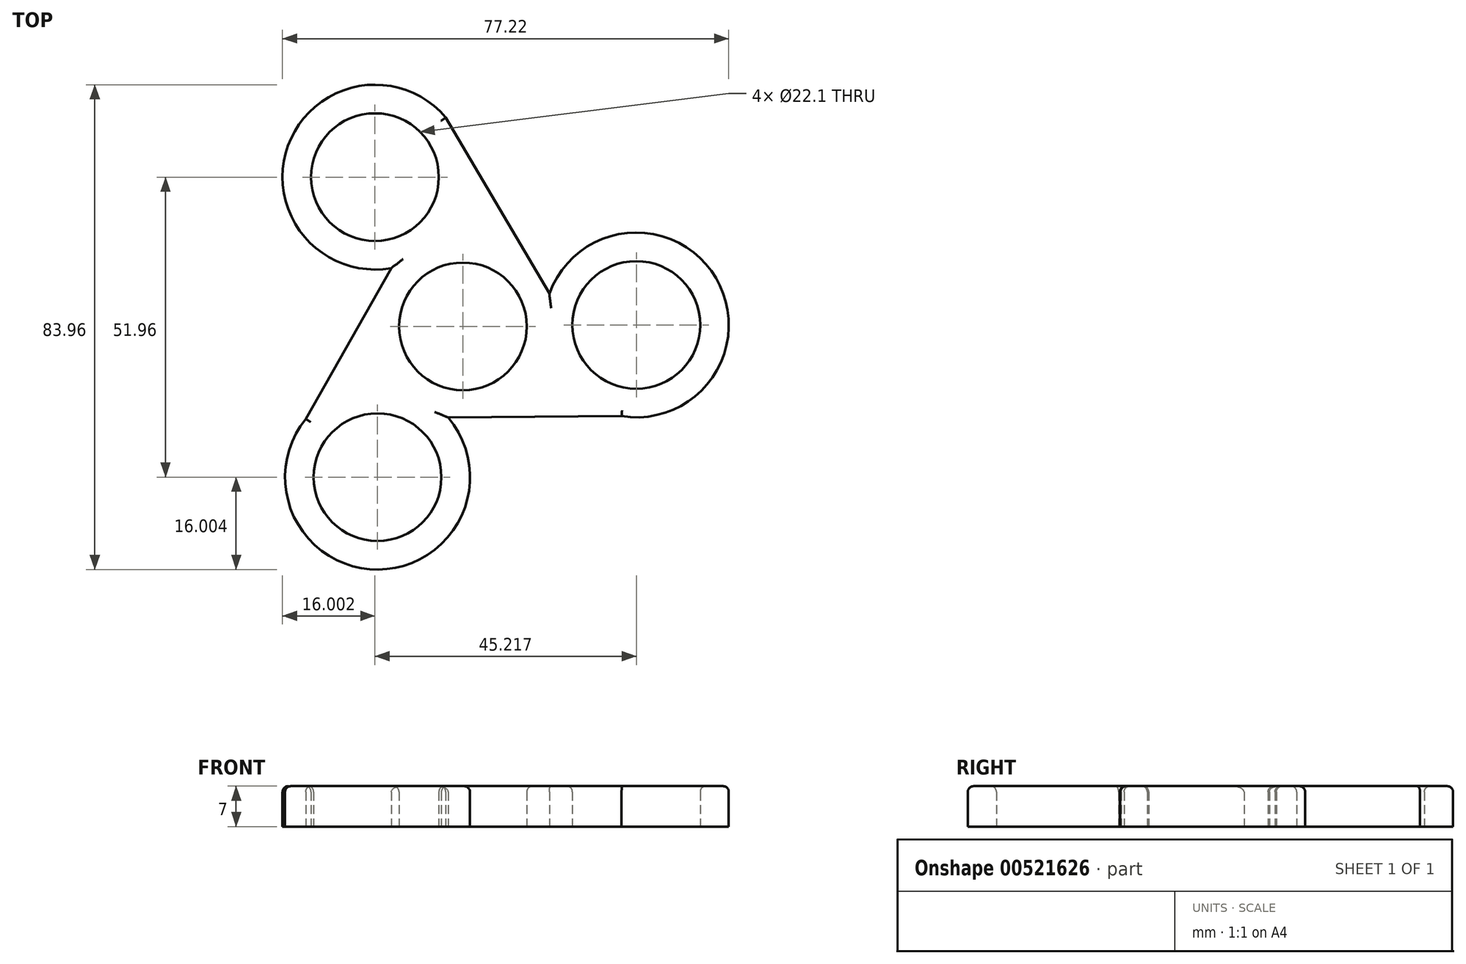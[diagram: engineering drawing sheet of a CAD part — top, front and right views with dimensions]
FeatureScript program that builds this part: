
annotation { "Feature Type Name" : "Feature", "Feature Type Description" : "" }
export const myFeature = defineFeature(function(context is Context, id is Id, definition is map)
    precondition{}
    {
        {
            var Q0;
            Q0=qCreatedBy(makeId("Top.planeOp"),FACE);
            var sketch = newSketch(context, id + "F0", { "sketchPlane" : qUnion([Q0])});
            skCircle(sketch, "E0", {"center": v(0, 0) * mm, "radius": 11.05 * mm});
            skCircle(sketch, "E1", {"center": v(0, 0) * mm, "radius": 16 * mm});
            skLineSegment(sketch, "E2", {"start": v(0, 0) * mm, "end": v(-14.78, -26.1) * mm});
            skLineSegment(sketch, "E3", {"start": v(0, 0) * mm, "end": v(30, 0.25) * mm});
            skLineSegment(sketch, "E4", {"start": v(0, 0) * mm, "end": v(-15.22, 25.85) * mm});
            skCircle(sketch, "E5", {"center": v(-15.22, 25.85) * mm, "radius": 11.05 * mm});
            skCircle(sketch, "E6", {"center": v(-14.78, -26.1) * mm, "radius": 11.05 * mm});
            skCircle(sketch, "E7", {"center": v(30, 0.25) * mm, "radius": 11.05 * mm});
            skCircle(sketch, "E8", {"center": v(-14.78, -26.1) * mm, "radius": 16 * mm});
            skCircle(sketch, "E9", {"center": v(-15.22, 25.85) * mm, "radius": 16 * mm});
            skCircle(sketch, "E10", {"center": v(30, 0.25) * mm, "radius": 16 * mm});
            skLineSegment(sketch, "E11", {"start": v(14.95, 5.7) * mm, "end": v(-2.98, 36.16) * mm});
            skLineSegment(sketch, "E12", {"start": v(-12.4, 10.1) * mm, "end": v(-27.19, -16) * mm});
            skLineSegment(sketch, "E13", {"start": v(-2.55, -15.8) * mm, "end": v(27.45, -15.54) * mm});
            skSolve(sketch);
        }
        {
            var Q0;
            {var subQ0=sQuery(id+"F0.wireOp",EDGE,"E4");var subQ1=sQuery(id+"F0.wireOp",EDGE,"E0");var subQ2=makeQuery(id+"F0.imprint","INTERSECT",VERTEX,{"derivedFrom":[subQ1,subQ0]});Q0=makeQuery(id+"F0.imprint","IMPRINT",FACE,{"disambiguationData":[TD([[makeQuery(id+"F0.imprint","IMPRINT",EDGE,{"disambiguationData":[TD([[subQ2,-1.0]])],"derivedFrom":subQ1}),-1.0]])]});}
            var Q1;
            Q1=makeQuery(id+"F0.imprint","IMPRINT",FACE,{"disambiguationData":[TD([[makeQuery(id+"F0.imprint","IMPRINT",EDGE,{"derivedFrom":sQuery(id+"F0.wireOp",EDGE,"E6")}),-1.0]])]});
            var Q2;
            {var subQ0=sQuery(id+"F0.wireOp",EDGE,"E12");var subQ1=sQuery(id+"F0.wireOp",EDGE,"E1");var subQ2=makeQuery(id+"F0.imprint","INTERSECT",VERTEX,{"derivedFrom":[subQ1,subQ0]});Q2=makeQuery(id+"F0.imprint","IMPRINT",FACE,{"disambiguationData":[TD([[makeQuery(id+"F0.imprint","IMPRINT",EDGE,{"disambiguationData":[TD([[subQ2,-1.0]])],"derivedFrom":subQ1}),-1.0]])]});}
            var Q3;
            {var subQ0=sQuery(id+"F0.wireOp",EDGE,"E3");var subQ1=sQuery(id+"F0.wireOp",EDGE,"E0");var subQ2=makeQuery(id+"F0.imprint","INTERSECT",VERTEX,{"derivedFrom":[subQ1,subQ0]});Q3=makeQuery(id+"F0.imprint","IMPRINT",FACE,{"disambiguationData":[TD([[makeQuery(id+"F0.imprint","IMPRINT",EDGE,{"disambiguationData":[TD([[subQ2,1.0]])],"derivedFrom":subQ1}),-1.0]])]});}
            var Q4;
            {var subQ1=sQuery(id+"F0.wireOp",EDGE,"E1");var subQ3=sQuery(id+"F0.wireOp",EDGE,"E2");var subQ4=makeQuery(id+"F0.imprint","INTERSECT",VERTEX,{"derivedFrom":[subQ1,subQ3]});Q4=makeQuery(id+"F0.imprint","IMPRINT",FACE,{"disambiguationData":[TD([[makeQuery(id+"F0.imprint","IMPRINT",EDGE,{"disambiguationData":[TD([[subQ4,1.0]])],"derivedFrom":subQ3}),1.0]])]});}
            var Q5;
            {var subQ0=sQuery(id+"F0.wireOp",EDGE,"E4");var subQ1=sQuery(id+"F0.wireOp",EDGE,"E0");var subQ2=makeQuery(id+"F0.imprint","INTERSECT",VERTEX,{"derivedFrom":[subQ1,subQ0]});Q5=makeQuery(id+"F0.imprint","IMPRINT",FACE,{"disambiguationData":[TD([[makeQuery(id+"F0.imprint","IMPRINT",EDGE,{"disambiguationData":[TD([[subQ2,1.0]])],"derivedFrom":subQ1}),-1.0]])]});}
            var Q6;
            {var subQ1=sQuery(id+"F0.wireOp",EDGE,"E1");var subQ3=sQuery(id+"F0.wireOp",EDGE,"E3");var subQ4=makeQuery(id+"F0.imprint","INTERSECT",VERTEX,{"derivedFrom":[subQ1,subQ3]});Q6=makeQuery(id+"F0.imprint","IMPRINT",FACE,{"disambiguationData":[TD([[makeQuery(id+"F0.imprint","IMPRINT",EDGE,{"disambiguationData":[TD([[subQ4,1.0]])],"derivedFrom":subQ3}),1.0]])]});}
            var Q7;
            Q7=makeQuery(id+"F0.imprint","IMPRINT",FACE,{"disambiguationData":[TD([[makeQuery(id+"F0.imprint","IMPRINT",EDGE,{"derivedFrom":sQuery(id+"F0.wireOp",EDGE,"E7")}),-1.0]])]});
            var Q8;
            Q8=makeQuery(id+"F0.imprint","IMPRINT",FACE,{"disambiguationData":[TD([[makeQuery(id+"F0.imprint","IMPRINT",EDGE,{"derivedFrom":sQuery(id+"F0.wireOp",EDGE,"E5")}),-1.0]])]});
            var Q9;
            {var subQ0=sQuery(id+"F0.wireOp",EDGE,"E11");var subQ1=sQuery(id+"F0.wireOp",EDGE,"E1");var subQ2=makeQuery(id+"F0.imprint","INTERSECT",VERTEX,{"derivedFrom":[subQ1,subQ0]});Q9=makeQuery(id+"F0.imprint","IMPRINT",FACE,{"disambiguationData":[TD([[makeQuery(id+"F0.imprint","IMPRINT",EDGE,{"disambiguationData":[TD([[subQ2,-1.0]])],"derivedFrom":subQ1}),-1.0]])]});}
            var Q10;
            {var subQ0=sQuery(id+"F0.wireOp",EDGE,"E13");var subQ1=sQuery(id+"F0.wireOp",EDGE,"E1");var subQ2=makeQuery(id+"F0.imprint","INTERSECT",VERTEX,{"derivedFrom":[subQ1,subQ0]});Q10=makeQuery(id+"F0.imprint","IMPRINT",FACE,{"disambiguationData":[TD([[makeQuery(id+"F0.imprint","IMPRINT",EDGE,{"disambiguationData":[TD([[subQ2,-1.0]])],"derivedFrom":subQ1}),-1.0]])]});}
            var Q11;
            {var subQ0=sQuery(id+"F0.wireOp",EDGE,"E3");var subQ1=sQuery(id+"F0.wireOp",EDGE,"E1");var subQ2=makeQuery(id+"F0.imprint","INTERSECT",VERTEX,{"derivedFrom":[subQ1,subQ0]});Q11=makeQuery(id+"F0.imprint","IMPRINT",FACE,{"disambiguationData":[TD([[makeQuery(id+"F0.imprint","IMPRINT",EDGE,{"disambiguationData":[TD([[subQ2,1.0]])],"derivedFrom":subQ1}),1.0]])]});}
            var Q12;
            {var subQ0=sQuery(id+"F0.wireOp",EDGE,"E2");var subQ1=sQuery(id+"F0.wireOp",EDGE,"E1");var subQ2=makeQuery(id+"F0.imprint","INTERSECT",VERTEX,{"derivedFrom":[subQ1,subQ0]});Q12=makeQuery(id+"F0.imprint","IMPRINT",FACE,{"disambiguationData":[TD([[makeQuery(id+"F0.imprint","IMPRINT",EDGE,{"disambiguationData":[TD([[subQ2,1.0]])],"derivedFrom":subQ1}),1.0]])]});}
            var Q13;
            {var subQ1=sQuery(id+"F0.wireOp",EDGE,"E1");var subQ3=sQuery(id+"F0.wireOp",EDGE,"E4");var subQ4=makeQuery(id+"F0.imprint","INTERSECT",VERTEX,{"derivedFrom":[subQ1,subQ3]});Q13=makeQuery(id+"F0.imprint","IMPRINT",FACE,{"disambiguationData":[TD([[makeQuery(id+"F0.imprint","IMPRINT",EDGE,{"disambiguationData":[TD([[subQ4,1.0]])],"derivedFrom":subQ3}),1.0]])]});}
            var Q14;
            {var subQ0=sQuery(id+"F0.wireOp",EDGE,"E4");var subQ1=sQuery(id+"F0.wireOp",EDGE,"E1");var subQ2=makeQuery(id+"F0.imprint","INTERSECT",VERTEX,{"derivedFrom":[subQ1,subQ0]});Q14=makeQuery(id+"F0.imprint","IMPRINT",FACE,{"disambiguationData":[TD([[makeQuery(id+"F0.imprint","IMPRINT",EDGE,{"disambiguationData":[TD([[subQ2,1.0]])],"derivedFrom":subQ1}),1.0]])]});}
            extrude(context, id + "F1", {"entities" : qUnion([Q0, Q1, Q2, Q3, Q4, Q5, Q6, Q7, Q8, Q9, Q10, Q11, Q12, Q13, Q14]), "depth" : 7 * mm, "offsetDistance" : 25 * mm});
        }
        {
            var Q0;
            Q0=makeQuery(id+"F1.opExtrude","CAP_FACE",FACE,{"disambiguationData":[OSD([sQuery(id+"F0.wireOp",EDGE,"E0"),sQuery(id+"F0.wireOp",EDGE,"E5"),sQuery(id+"F0.wireOp",EDGE,"E6"),sQuery(id+"F0.wireOp",EDGE,"E7"),sQuery(id+"F0.wireOp",EDGE,"E8"),sQuery(id+"F0.wireOp",EDGE,"E9"),sQuery(id+"F0.wireOp",EDGE,"E10"),sQuery(id+"F0.wireOp",EDGE,"E11"),sQuery(id+"F0.wireOp",EDGE,"E12"),sQuery(id+"F0.wireOp",EDGE,"E13")])],"isStart":false});
            fillet(context, id + "F2", {"entities" : qUnion([Q0]), "radius" : 1 * mm, "tangentPropagation" : true, "allowEdgeOverflow" : false});
        }
    });
